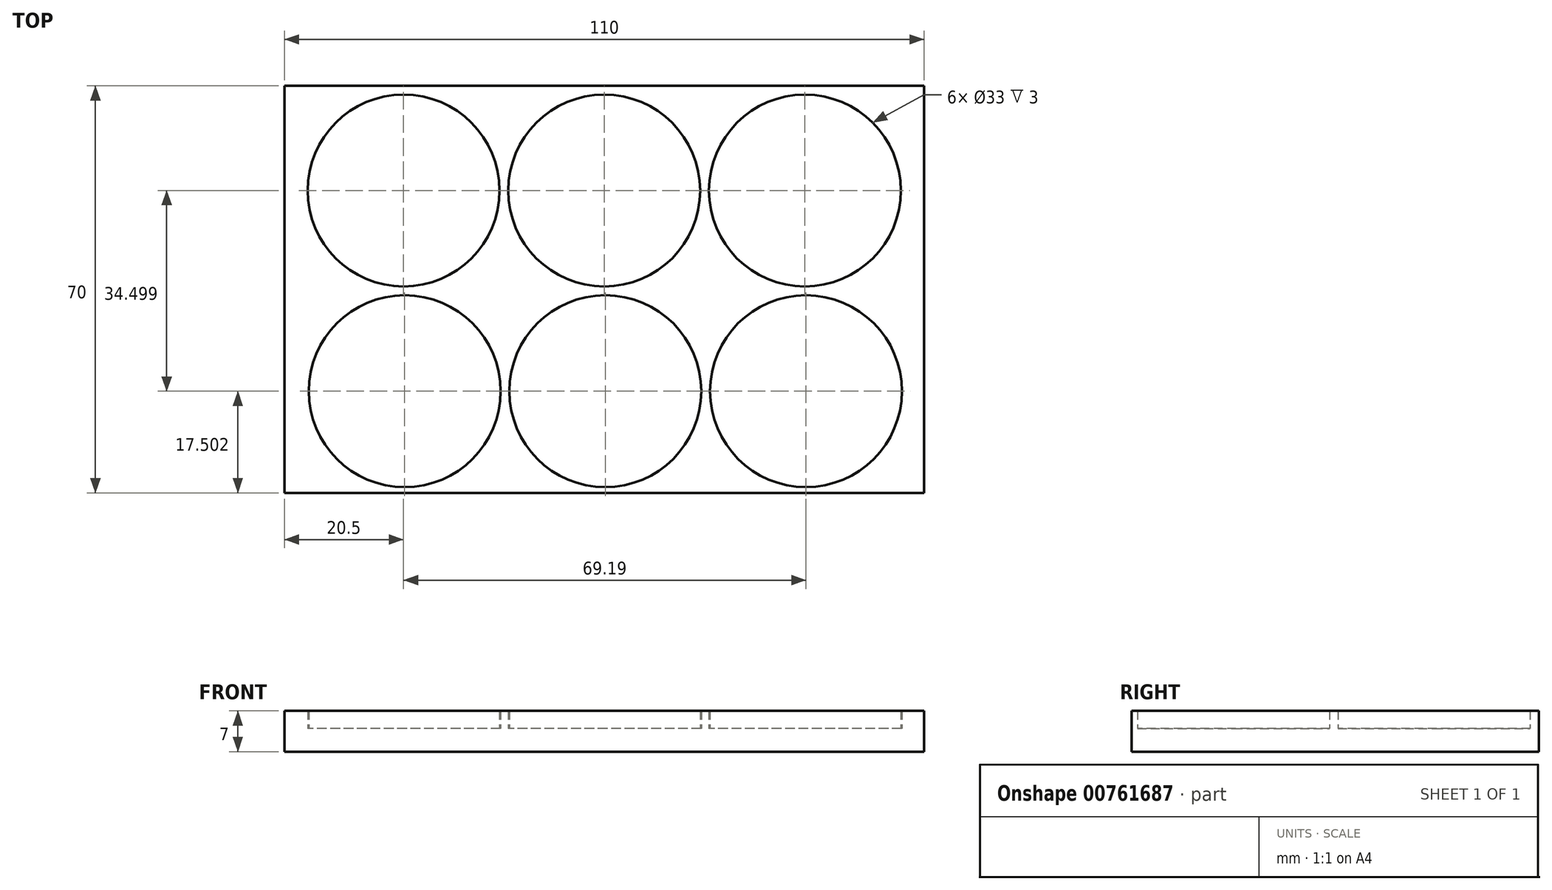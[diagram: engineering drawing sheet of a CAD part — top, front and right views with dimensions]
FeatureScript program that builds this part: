
annotation { "Feature Type Name" : "Feature", "Feature Type Description" : "" }
export const myFeature = defineFeature(function(context is Context, id is Id, definition is map)
    precondition{}
    {
        {
            var Q0;
            Q0=qCreatedBy(makeId("Top.planeOp"),FACE);
            var sketch = newSketch(context, id + "F0", { "sketchPlane" : qUnion([Q0])});
            skCircle(sketch, "E0", {"center": v(0, 50.52) * mm, "radius": 16.5 * mm});
            skLineSegment(sketch, "E1.bottom", {"start": v(55, -1.48) * mm, "end": v(-55, -1.48) * mm});
            skLineSegment(sketch, "E1.top", {"start": v(55, 68.52) * mm, "end": v(-55, 68.52) * mm});
            skLineSegment(sketch, "E1.left", {"start": v(55, -1.48) * mm, "end": v(55, 68.52) * mm});
            skLineSegment(sketch, "E1.right", {"start": v(-55, -1.48) * mm, "end": v(-55, 68.52) * mm});
            skPoint(sketch, "E1.middle", {"position": v(0, 33.52) * mm});
            skCircle(sketch, "E2", {"center": v(34.5, 50.52) * mm, "radius": 16.5 * mm});
            skCircle(sketch, "E3", {"center": v(0.19, 16.02) * mm, "radius": 16.5 * mm});
            skCircle(sketch, "E4", {"center": v(34.69, 16.02) * mm, "radius": 16.5 * mm});
            skCircle(sketch, "E5", {"center": v(-34.5, 50.52) * mm, "radius": 16.5 * mm});
            skCircle(sketch, "E6", {"center": v(-34.31, 16.02) * mm, "radius": 16.5 * mm});
            skSolve(sketch);
        }
        {
            var Q0;
            Q0=makeQuery(id+"F0.imprint","IMPRINT",FACE,{"disambiguationData":[TD([[makeQuery(id+"F0.imprint","IMPRINT",EDGE,{"derivedFrom":sQuery(id+"F0.wireOp",EDGE,"E0")}),-1.0]])]});
            extrude(context, id + "F1", {"entities" : qUnion([Q0]), "depth" : 7 * mm, "offsetDistance" : 25 * mm});
        }
        {
            var Q0;
            Q0=makeQuery(id+"F0.imprint","IMPRINT",FACE,{"disambiguationData":[TD([[makeQuery(id+"F0.imprint","IMPRINT",EDGE,{"derivedFrom":sQuery(id+"F0.wireOp",EDGE,"E5")}),1.0]])]});
            var Q1;
            Q1=makeQuery(id+"F0.imprint","IMPRINT",FACE,{"disambiguationData":[TD([[makeQuery(id+"F0.imprint","IMPRINT",EDGE,{"derivedFrom":sQuery(id+"F0.wireOp",EDGE,"E0")}),1.0]])]});
            var Q2;
            Q2=makeQuery(id+"F0.imprint","IMPRINT",FACE,{"disambiguationData":[TD([[makeQuery(id+"F0.imprint","IMPRINT",EDGE,{"derivedFrom":sQuery(id+"F0.wireOp",EDGE,"E2")}),1.0]])]});
            var Q3;
            Q3=makeQuery(id+"F0.imprint","IMPRINT",FACE,{"disambiguationData":[TD([[makeQuery(id+"F0.imprint","IMPRINT",EDGE,{"derivedFrom":sQuery(id+"F0.wireOp",EDGE,"E4")}),1.0]])]});
            var Q4;
            Q4=makeQuery(id+"F0.imprint","IMPRINT",FACE,{"disambiguationData":[TD([[makeQuery(id+"F0.imprint","IMPRINT",EDGE,{"derivedFrom":sQuery(id+"F0.wireOp",EDGE,"E3")}),1.0]])]});
            var Q5;
            Q5=makeQuery(id+"F0.imprint","IMPRINT",FACE,{"disambiguationData":[TD([[makeQuery(id+"F0.imprint","IMPRINT",EDGE,{"derivedFrom":sQuery(id+"F0.wireOp",EDGE,"E6")}),1.0]])]});
            extrude(context, id + "F2", {"entities" : qUnion([Q0, Q1, Q2, Q3, Q4, Q5]), "operationType" : NewBodyOperationType.ADD, "depth" : 4 * mm, "offsetDistance" : 25 * mm});
        }
    });
